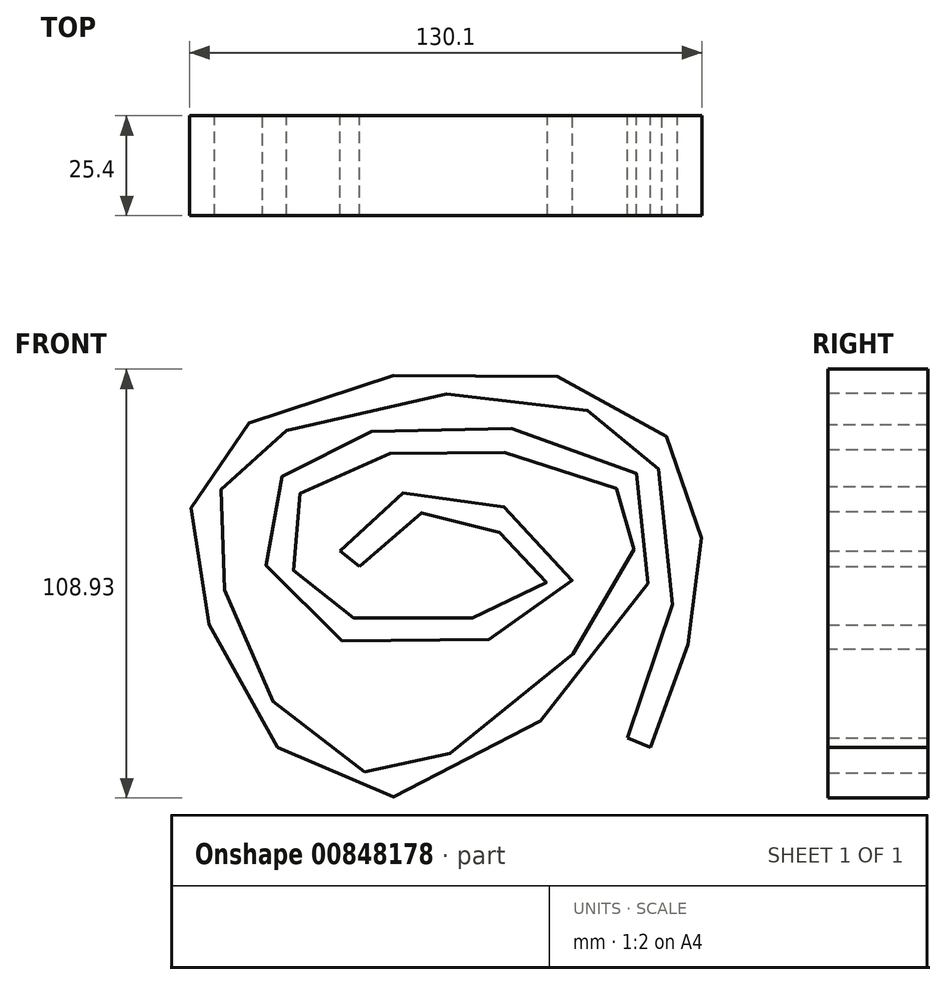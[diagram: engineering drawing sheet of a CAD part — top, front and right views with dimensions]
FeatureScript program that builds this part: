
annotation { "Feature Type Name" : "Feature", "Feature Type Description" : "" }
export const myFeature = defineFeature(function(context is Context, id is Id, definition is map)
    precondition{}
    {
        {
            var Q0;
            Q0=qCreatedBy(makeId("Front.planeOp"),FACE);
            var sketch = newSketch(context, id + "F0", { "sketchPlane" : qUnion([Q0])});
            skFitSpline(sketch, "E0", {"points": [v(-35.8, 26.47) * mm, v(-10.52, 42.78) * mm, v(23.05, 17.5) * mm, v(-39.35, 5.2) * mm, v(-53.77, 39.95) * mm, v(-14.06, 58.38) * mm, v(45.74, 34.98) * mm, v(-23.75, -36.16) * mm, v(-70.8, 13.47) * mm, v(-61.57, 57.2) * mm, v(33.45, 66.42) * mm, v(56.14, 24.82) * mm, v(43.14, -23.4) * mm], "startDerivative": vector(324, 416.68) * mm, "endDerivative": vector(-240.58, -598.62) * mm});
            skFitSpline(sketch, "E1.0", {"points": [v(-30.8, 22.58) * mm, v(-29.95, 23.66) * mm, v(-28.3, 25.78) * mm, v(-25.89, 28.7) * mm, v(-23.5, 31.24) * mm, v(-21.12, 33.3) * mm, v(-18.75, 34.86) * mm, v(-16.73, 35.73) * mm, v(-15, 36.2) * mm, v(-13.62, 36.42) * mm, v(-12.36, 36.49) * mm, v(-11.28, 36.47) * mm, v(-10.15, 36.4) * mm, v(-8.58, 36.2) * mm, v(-5.84, 35.62) * mm, v(-2.11, 34.46) * mm, v(2.48, 32.46) * mm, v(6.89, 30) * mm, v(10.82, 27.21) * mm, v(13.44, 24.82) * mm, v(15.02, 23) * mm, v(15.92, 21.73) * mm, v(16.5, 20.64) * mm, v(16.8, 19.79) * mm, v(16.88, 19.33) * mm, v(16.88, 19.1) * mm, v(16.87, 18.96) * mm, v(16.85, 18.86) * mm, v(16.8, 18.7) * mm, v(16.7, 18.48) * mm, v(16.46, 18.08) * mm, v(15.95, 17.43) * mm, v(14.95, 16.49) * mm, v(13.57, 15.45) * mm, v(11.83, 14.4) * mm, v(9.77, 13.35) * mm, v(6.65, 12.02) * mm, v(2.17, 10.53) * mm, v(-3.87, 9.13) * mm, v(-10.3, 8.2) * mm, v(-16.83, 7.77) * mm, v(-23.22, 7.91) * mm, v(-28.18, 8.52) * mm, v(-31.8, 9.3) * mm, v(-34.3, 10.01) * mm, v(-36.17, 10.72) * mm, v(-37.52, 11.34) * mm, v(-38.82, 12) * mm, v(-40.3, 12.92) * mm, v(-42.43, 14.52) * mm, v(-44.66, 16.78) * mm, v(-46.71, 19.83) * mm, v(-48.18, 23.15) * mm, v(-49.05, 26.63) * mm, v(-49.35, 30.13) * mm, v(-49.14, 32.95) * mm, v(-48.72, 35.06) * mm, v(-48.29, 36.56) * mm, v(-47.75, 37.94) * mm, v(-46.9, 39.65) * mm, v(-45.55, 41.6) * mm, v(-43.45, 43.71) * mm, v(-40.78, 45.65) * mm, v(-37.51, 47.38) * mm, v(-33.65, 48.88) * mm, v(-29.2, 50.12) * mm, v(-24.22, 51.07) * mm, v(-19.66, 51.63) * mm, v(-15.78, 51.94) * mm, v(-11.75, 52.15) * mm, v(-6.48, 52.23) * mm, v(0.02, 52.02) * mm, v(6.54, 51.46) * mm, v(12.91, 50.54) * mm, v(18.96, 49.24) * mm, v(24.5, 47.57) * mm, v(29.35, 45.53) * mm, v(33.35, 43.17) * mm, v(35.84, 41.04) * mm, v(37.32, 39.28) * mm, v(38.2, 37.94) * mm, v(38.84, 36.56) * mm, v(39.22, 35.34) * mm, v(39.43, 34.3) * mm, v(39.56, 33.2) * mm, v(39.6, 31.67) * mm, v(39.4, 29.56) * mm, v(38.96, 27.23) * mm, v(38.24, 24.72) * mm, v(36.93, 21.14) * mm, v(34.66, 16.36) * mm, v(31.02, 10.34) * mm, v(26.57, 4.23) * mm, v(21.46, -1.81) * mm, v(13.93, -9.56) * mm, v(5.6, -16.55) * mm, v(-2.94, -22.2) * mm, v(-9.3, -25.64) * mm, v(-14.4, -27.73) * mm, v(-18.29, -28.89) * mm, v(-21.07, -29.5) * mm, v(-23.25, -29.78) * mm, v(-24.91, -29.87) * mm, v(-26.54, -29.88) * mm, v(-28.5, -29.75) * mm, v(-31.55, -29.22) * mm, v(-35.19, -28.03) * mm, v(-39.39, -25.75) * mm, v(-43.42, -22.67) * mm, v(-48.53, -17.58) * mm, v(-53.14, -11.22) * mm, v(-57.12, -4.1) * mm, v(-59.77, 1.49) * mm, v(-62.07, 7.17) * mm, v(-63.69, 11.88) * mm, v(-64.8, 15.57) * mm, v(-65.78, 19.15) * mm, v(-66.75, 23.42) * mm, v(-67.45, 28.18) * mm, v(-67.68, 32.54) * mm, v(-67.42, 36.5) * mm, v(-66.68, 40.09) * mm, v(-65.44, 43.34) * mm, v(-63.67, 46.37) * mm, v(-61.65, 48.78) * mm, v(-59.63, 50.66) * mm, v(-57.9, 52.05) * mm, v(-55.94, 53.41) * mm, v(-53, 55.2) * mm, v(-48.79, 57.32) * mm, v(-42.99, 59.64) * mm, v(-34.47, 62.34) * mm, v(-22.67, 64.9) * mm, v(-7.73, 66.47) * mm, v(4.5, 66.4) * mm, v(13.63, 65.47) * mm, v(20, 64.33) * mm, v(24.82, 63.01) * mm, v(28.3, 61.76) * mm, v(30.7, 60.73) * mm, v(32.88, 59.6) * mm, v(35.58, 57.97) * mm, v(38.53, 55.71) * mm, v(41.5, 52.67) * mm, v(43.95, 49.32) * mm, v(45.94, 45.68) * mm, v(48.03, 40.47) * mm, v(49.6, 33.37) * mm, v(49.99, 24.38) * mm, v(49.1, 15.44) * mm, v(47.16, 6.47) * mm, v(44.37, -2.58) * mm, v(40.98, -11.73) * mm, v(38.5, -17.91) * mm, v(37.24, -21.03) * mm]});
            skLineSegment(sketch, "E2", {"start": v(-35.8, 26.47) * mm, "end": v(-30.8, 22.58) * mm});
            skLineSegment(sketch, "E3", {"start": v(37.24, -21.03) * mm, "end": v(43.14, -23.4) * mm});
            skSolve(sketch);
        }
        {
            var Q0;
            Q0=makeQuery(id+"F0.imprint","IMPRINT",FACE,{"disambiguationData":[TD([[makeQuery(id+"F0.imprint","IMPRINT",EDGE,{"derivedFrom":sQuery(id+"F0.wireOp",EDGE,"E0")}),-1.0]])]});
            extrude(context, id + "F1", {"entities" : qUnion([Q0]), "depth" : 25.4 * mm, "offsetDistance" : 25.4 * mm});
        }
    });
